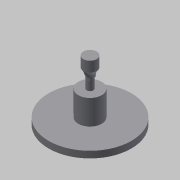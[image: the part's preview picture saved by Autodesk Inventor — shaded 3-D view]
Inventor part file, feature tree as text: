
AUTODESK INVENTOR PART (.ipt)
format: ipt  version: 2018 (Build 220112000, 112)  size: 178,176 bytes
history: native  units: mm
features: other x10, plane x8, sketch x5, extrude x3, projected_geometry x3
ambient origin geometry x8: Origin, YZ Plane, XZ Plane, XY Plane, X Axis, Y Axis, Z Axis, Center Point
bodies: Body1 (feature_tree)
feature tree (29):
  other  "零件1.ipt"
  plane  "工作平面1"
  other  "直接編輯1"
  plane  "工作平面2"
  plane  "工作平面3"
  extrude  "擠出2"  Depth=1.0mm
  other  "刪除面1"
  plane  "工作平面4"
  plane  "工作平面5"
  plane  "工作平面8"
  extrude  "擠出3"  [1 undecoded]
  extrude  "擠出4"  TaperAngle=0.0deg  [1 undecoded]
  other  "迴轉1"
  other  "迴轉2"
  other  "刪除面2"
  other  "實體1::零件1.ipt"
  other  "標籤特徵1"
  sketch  "草圖2"
  projected_geometry  "投影迴路1"
  plane  "工作平面6"
  plane  "工作平面7"
  sketch  "草圖3"
  projected_geometry  "投影迴路2"
  sketch  "草圖4"
  projected_geometry  "投影迴路3"
  sketch  "草圖5"
  sketch  "草圖6"
  other  "實體1"
  other  "移動1"
note: 2 required parameter values undecoded (feature->parameter linkage not recoverable at this tier; creation-order binding heuristic only, values carry confidence <= 0.55)
